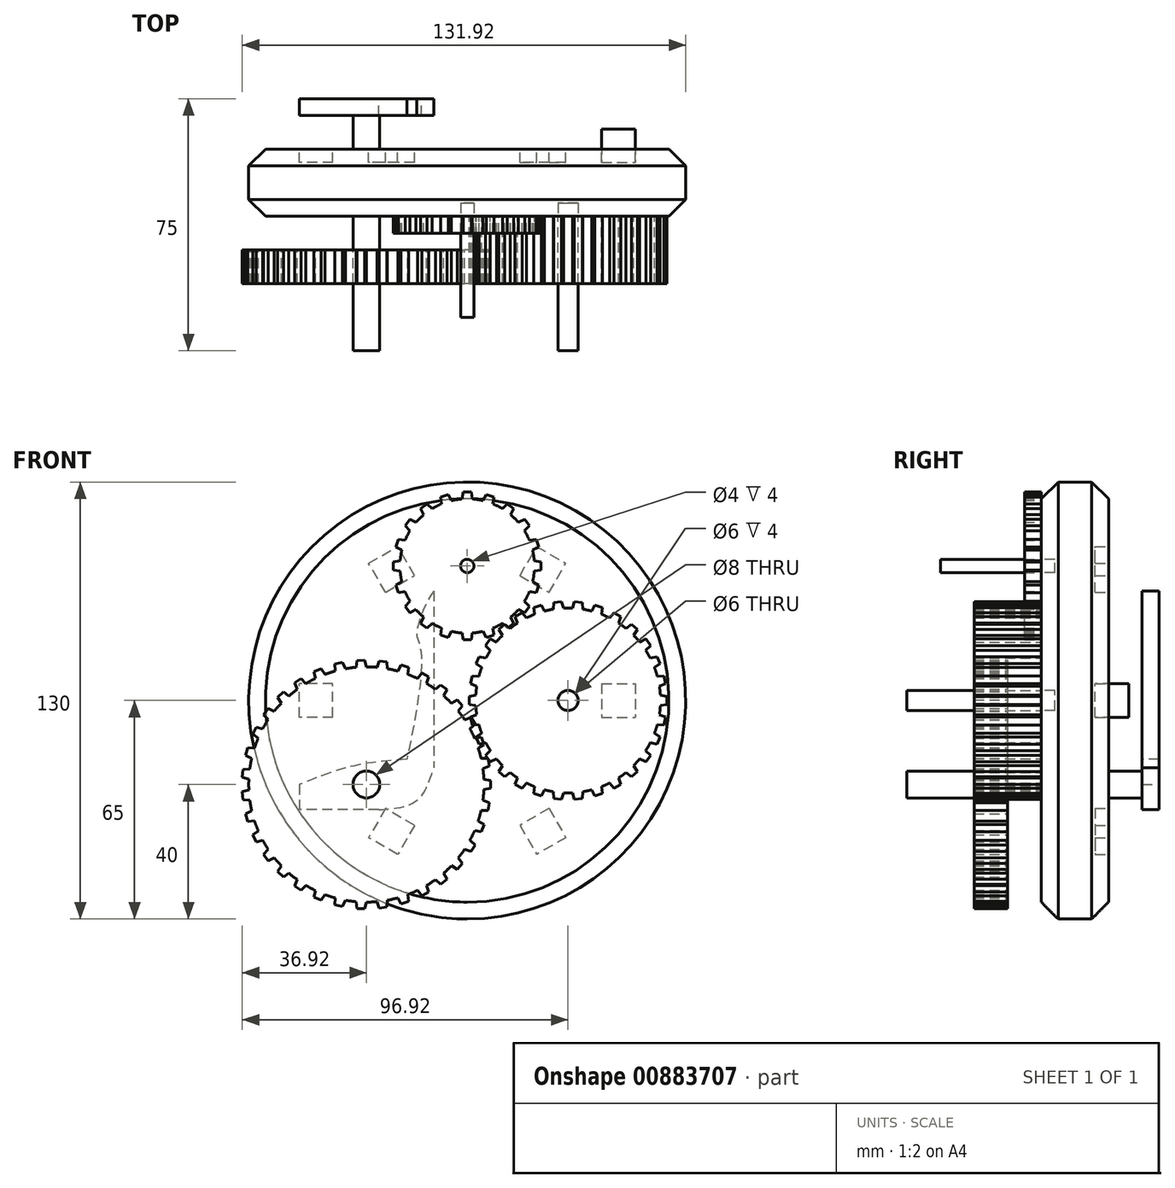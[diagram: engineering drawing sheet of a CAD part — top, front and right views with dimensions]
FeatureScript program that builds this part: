
annotation { "Feature Type Name" : "Feature", "Feature Type Description" : "" }
export const myFeature = defineFeature(function(context is Context, id is Id, definition is map)
    precondition{}
    {
        {
            var Q0;
            Q0=qCreatedBy(makeId("Front.planeOp"),FACE);
            var sketch = newSketch(context, id + "F0", { "sketchPlane" : qUnion([Q0])});
            skCircle(sketch, "E0", {"center": v(0, 0) * mm, "radius": 65 * mm});
            skSolve(sketch);
        }
        {
            var Q0;
            Q0 = qSketchRegion(id + "F0", true);
            extrude(context, id + "F1", {"entities" : qUnion([Q0]), "depth" : 20 * mm, "offsetDistance" : 25 * mm});
        }
        {
            var Q0;
            Q0=makeQuery(id+"F1.opExtrude","CAP_FACE",FACE,{"disambiguationData":[OSD([sQuery(id+"F0.wireOp",EDGE,"E0")])],"isStart":false});
            var sketch = newSketch(context, id + "F2", { "sketchPlane" : qUnion([Q0])});
            skCircle(sketch, "E1", {"center": v(0, 40) * mm, "radius": 20 * mm});
            skCircle(sketch, "E2.0", {"center": v(0, 40) * mm, "radius": 2 * mm});
            skLineSegment(sketch, "E3", {"start": v(0, 61.97) * mm, "end": v(1.18, 61.97) * mm});
            skLineSegment(sketch, "E4", {"start": v(1.18, 61.97) * mm, "end": v(1.54, 59.94) * mm});
            skLineSegment(sketch, "E5.MirrorCS", {"start": v(0, 61.97) * mm, "end": v(-1.18, 61.97) * mm});
            skLineSegment(sketch, "E6.MirrorCS", {"start": v(-1.18, 61.97) * mm, "end": v(-1.54, 59.94) * mm});
            skLineSegment(sketch, "E7.1.0", {"start": v(-7.9, 60.53) * mm, "end": v(-7.62, 58.5) * mm});
            skLineSegment(sketch, "E7.1.1", {"start": v(-6.79, 60.9) * mm, "end": v(-7.9, 60.53) * mm});
            skLineSegment(sketch, "E7.1.2", {"start": v(-6.79, 60.9) * mm, "end": v(-5.67, 61.26) * mm});
            skLineSegment(sketch, "E7.1.3", {"start": v(-5.67, 61.26) * mm, "end": v(-4.7, 59.44) * mm});
            skLineSegment(sketch, "E7.2.0", {"start": v(-13.87, 57.08) * mm, "end": v(-12.96, 55.23) * mm});
            skLineSegment(sketch, "E7.2.1", {"start": v(-12.91, 57.77) * mm, "end": v(-13.87, 57.08) * mm});
            skLineSegment(sketch, "E7.2.2", {"start": v(-12.91, 57.77) * mm, "end": v(-11.96, 58.47) * mm});
            skLineSegment(sketch, "E7.2.3", {"start": v(-11.96, 58.47) * mm, "end": v(-10.48, 57.04) * mm});
            skLineSegment(sketch, "E8.2.3.0", {"start": v(-18.47, 51.96) * mm, "end": v(-17.04, 50.48) * mm});
            skLineSegment(sketch, "E8.3.3.0", {"start": v(-17.77, 52.91) * mm, "end": v(-18.47, 51.96) * mm});
            skLineSegment(sketch, "E8.6.3.0", {"start": v(-17.77, 52.91) * mm, "end": v(-17.08, 53.87) * mm});
            skLineSegment(sketch, "E8.9.3.0", {"start": v(-17.08, 53.87) * mm, "end": v(-15.23, 52.96) * mm});
            skLineSegment(sketch, "E8.2.4.0", {"start": v(-21.26, 45.67) * mm, "end": v(-19.44, 44.7) * mm});
            skLineSegment(sketch, "E8.3.4.0", {"start": v(-20.9, 46.79) * mm, "end": v(-21.26, 45.67) * mm});
            skLineSegment(sketch, "E8.6.4.0", {"start": v(-20.9, 46.79) * mm, "end": v(-20.53, 47.9) * mm});
            skLineSegment(sketch, "E8.9.4.0", {"start": v(-20.53, 47.9) * mm, "end": v(-18.5, 47.62) * mm});
            skLineSegment(sketch, "E8.2.5.0", {"start": v(-21.97, 38.82) * mm, "end": v(-19.94, 38.46) * mm});
            skLineSegment(sketch, "E8.3.5.0", {"start": v(-21.97, 40) * mm, "end": v(-21.97, 38.82) * mm});
            skLineSegment(sketch, "E8.6.5.0", {"start": v(-21.97, 40) * mm, "end": v(-21.97, 41.18) * mm});
            skLineSegment(sketch, "E8.9.5.0", {"start": v(-21.97, 41.18) * mm, "end": v(-19.94, 41.54) * mm});
            skLineSegment(sketch, "E8.2.6.0", {"start": v(-20.53, 32.1) * mm, "end": v(-18.5, 32.38) * mm});
            skLineSegment(sketch, "E8.3.6.0", {"start": v(-20.9, 33.21) * mm, "end": v(-20.53, 32.1) * mm});
            skLineSegment(sketch, "E8.6.6.0", {"start": v(-20.9, 33.21) * mm, "end": v(-21.26, 34.33) * mm});
            skLineSegment(sketch, "E8.9.6.0", {"start": v(-21.26, 34.33) * mm, "end": v(-19.44, 35.3) * mm});
            skLineSegment(sketch, "E8.2.7.0", {"start": v(-17.08, 26.13) * mm, "end": v(-15.23, 27.04) * mm});
            skLineSegment(sketch, "E8.3.7.0", {"start": v(-17.77, 27.09) * mm, "end": v(-17.08, 26.13) * mm});
            skLineSegment(sketch, "E8.6.7.0", {"start": v(-17.77, 27.09) * mm, "end": v(-18.47, 28.04) * mm});
            skLineSegment(sketch, "E8.9.7.0", {"start": v(-18.47, 28.04) * mm, "end": v(-17.04, 29.52) * mm});
            skLineSegment(sketch, "E8.2.8.0", {"start": v(-11.96, 21.53) * mm, "end": v(-10.48, 22.96) * mm});
            skLineSegment(sketch, "E8.3.8.0", {"start": v(-12.91, 22.23) * mm, "end": v(-11.96, 21.53) * mm});
            skLineSegment(sketch, "E8.6.8.0", {"start": v(-12.91, 22.23) * mm, "end": v(-13.87, 22.92) * mm});
            skLineSegment(sketch, "E8.9.8.0", {"start": v(-13.87, 22.92) * mm, "end": v(-12.96, 24.77) * mm});
            skLineSegment(sketch, "E8.2.9.0", {"start": v(-5.67, 18.74) * mm, "end": v(-4.7, 20.56) * mm});
            skLineSegment(sketch, "E8.3.9.0", {"start": v(-6.79, 19.1) * mm, "end": v(-5.67, 18.74) * mm});
            skLineSegment(sketch, "E8.6.9.0", {"start": v(-6.79, 19.1) * mm, "end": v(-7.9, 19.47) * mm});
            skLineSegment(sketch, "E8.9.9.0", {"start": v(-7.9, 19.47) * mm, "end": v(-7.62, 21.5) * mm});
            skLineSegment(sketch, "E9.2.10.0", {"start": v(1.18, 18.03) * mm, "end": v(1.54, 20.06) * mm});
            skLineSegment(sketch, "E9.3.10.0", {"start": v(0, 18.03) * mm, "end": v(1.18, 18.03) * mm});
            skLineSegment(sketch, "E9.6.10.0", {"start": v(0, 18.03) * mm, "end": v(-1.18, 18.03) * mm});
            skLineSegment(sketch, "E9.9.10.0", {"start": v(-1.18, 18.03) * mm, "end": v(-1.54, 20.06) * mm});
            skLineSegment(sketch, "E9.2.11.0", {"start": v(7.9, 19.47) * mm, "end": v(7.62, 21.5) * mm});
            skLineSegment(sketch, "E9.3.11.0", {"start": v(6.79, 19.1) * mm, "end": v(7.9, 19.47) * mm});
            skLineSegment(sketch, "E9.6.11.0", {"start": v(6.79, 19.1) * mm, "end": v(5.67, 18.74) * mm});
            skLineSegment(sketch, "E9.9.11.0", {"start": v(5.67, 18.74) * mm, "end": v(4.7, 20.56) * mm});
            skLineSegment(sketch, "E9.2.12.0", {"start": v(13.87, 22.92) * mm, "end": v(12.96, 24.77) * mm});
            skLineSegment(sketch, "E9.3.12.0", {"start": v(12.91, 22.23) * mm, "end": v(13.87, 22.92) * mm});
            skLineSegment(sketch, "E9.6.12.0", {"start": v(12.91, 22.23) * mm, "end": v(11.96, 21.53) * mm});
            skLineSegment(sketch, "E9.9.12.0", {"start": v(11.96, 21.53) * mm, "end": v(10.48, 22.96) * mm});
            skLineSegment(sketch, "E9.2.13.0", {"start": v(18.47, 28.04) * mm, "end": v(17.04, 29.52) * mm});
            skLineSegment(sketch, "E9.3.13.0", {"start": v(17.77, 27.09) * mm, "end": v(18.47, 28.04) * mm});
            skLineSegment(sketch, "E9.6.13.0", {"start": v(17.77, 27.09) * mm, "end": v(17.08, 26.13) * mm});
            skLineSegment(sketch, "E9.9.13.0", {"start": v(17.08, 26.13) * mm, "end": v(15.23, 27.04) * mm});
            skLineSegment(sketch, "E9.2.14.0", {"start": v(21.26, 34.33) * mm, "end": v(19.44, 35.3) * mm});
            skLineSegment(sketch, "E9.3.14.0", {"start": v(20.9, 33.21) * mm, "end": v(21.26, 34.33) * mm});
            skLineSegment(sketch, "E9.6.14.0", {"start": v(20.9, 33.21) * mm, "end": v(20.53, 32.1) * mm});
            skLineSegment(sketch, "E9.9.14.0", {"start": v(20.53, 32.1) * mm, "end": v(18.5, 32.38) * mm});
            skLineSegment(sketch, "E9.2.15.0", {"start": v(21.97, 41.18) * mm, "end": v(19.94, 41.54) * mm});
            skLineSegment(sketch, "E9.3.15.0", {"start": v(21.97, 40) * mm, "end": v(21.97, 41.18) * mm});
            skLineSegment(sketch, "E9.6.15.0", {"start": v(21.97, 40) * mm, "end": v(21.97, 38.82) * mm});
            skLineSegment(sketch, "E9.9.15.0", {"start": v(21.97, 38.82) * mm, "end": v(19.94, 38.46) * mm});
            skLineSegment(sketch, "E9.2.16.0", {"start": v(20.53, 47.9) * mm, "end": v(18.5, 47.62) * mm});
            skLineSegment(sketch, "E9.3.16.0", {"start": v(20.9, 46.79) * mm, "end": v(20.53, 47.9) * mm});
            skLineSegment(sketch, "E9.6.16.0", {"start": v(20.9, 46.79) * mm, "end": v(21.26, 45.67) * mm});
            skLineSegment(sketch, "E9.9.16.0", {"start": v(21.26, 45.67) * mm, "end": v(19.44, 44.7) * mm});
            skLineSegment(sketch, "E9.2.17.0", {"start": v(17.08, 53.87) * mm, "end": v(15.23, 52.96) * mm});
            skLineSegment(sketch, "E9.3.17.0", {"start": v(17.77, 52.91) * mm, "end": v(17.08, 53.87) * mm});
            skLineSegment(sketch, "E9.6.17.0", {"start": v(17.77, 52.91) * mm, "end": v(18.47, 51.96) * mm});
            skLineSegment(sketch, "E9.9.17.0", {"start": v(18.47, 51.96) * mm, "end": v(17.04, 50.48) * mm});
            skLineSegment(sketch, "E9.2.18.0", {"start": v(11.96, 58.47) * mm, "end": v(10.48, 57.04) * mm});
            skLineSegment(sketch, "E9.3.18.0", {"start": v(12.91, 57.77) * mm, "end": v(11.96, 58.47) * mm});
            skLineSegment(sketch, "E9.6.18.0", {"start": v(12.91, 57.77) * mm, "end": v(13.87, 57.08) * mm});
            skLineSegment(sketch, "E9.9.18.0", {"start": v(13.87, 57.08) * mm, "end": v(12.96, 55.23) * mm});
            skLineSegment(sketch, "E9.2.19.0", {"start": v(5.67, 61.26) * mm, "end": v(4.7, 59.44) * mm});
            skLineSegment(sketch, "E9.3.19.0", {"start": v(6.79, 60.9) * mm, "end": v(5.67, 61.26) * mm});
            skLineSegment(sketch, "E9.6.19.0", {"start": v(6.79, 60.9) * mm, "end": v(7.9, 60.53) * mm});
            skLineSegment(sketch, "E9.9.19.0", {"start": v(7.9, 60.53) * mm, "end": v(7.62, 58.5) * mm});
            skSolve(sketch);
        }
        {
            var Q0;
            Q0 = qSketchRegion(id + "F2", true);
            extrude(context, id + "F3", {"entities" : qUnion([Q0]), "depth" : 5 * mm, "offsetDistance" : 25 * mm});
        }
        {
            var Q0;
            Q0=makeQuery(id+"F1.opExtrude","CAP_FACE",FACE,{"disambiguationData":[OSD([sQuery(id+"F0.wireOp",EDGE,"E0")])],"isStart":false});
            var sketch = newSketch(context, id + "F4", { "sketchPlane" : qUnion([Q0])});
            skCircle(sketch, "E10.0", {"center": v(0, 40) * mm, "radius": 2 * mm});
            skSolve(sketch);
        }
        {
            var Q0;
            Q0 = qSketchRegion(id + "F4", true);
            extrude(context, id + "F5", {"entities" : qUnion([Q0]), "depth" : 30 * mm, "offsetDistance" : 25 * mm});
        }
        {
            var Q0;
            Q0=makeQuery(id+"F1.opExtrude","CAP_FACE",FACE,{"disambiguationData":[OSD([sQuery(id+"F0.wireOp",EDGE,"E0")])],"isStart":false});
            var sketch = newSketch(context, id + "F6", { "sketchPlane" : qUnion([Q0])});
            skCircle(sketch, "E11", {"center": v(30, 0) * mm, "radius": 27.5 * mm});
            skLineSegment(sketch, "E12", {"start": v(59.46, 0) * mm, "end": v(59.46, -1.18) * mm});
            skLineSegment(sketch, "E13", {"start": v(59.46, -1.18) * mm, "end": v(57.46, -1.53) * mm});
            skLineSegment(sketch, "E14.MirrorCS", {"start": v(59.46, 0) * mm, "end": v(59.46, 1.18) * mm});
            skLineSegment(sketch, "E15.MirrorCS", {"start": v(59.46, 1.18) * mm, "end": v(57.46, 1.53) * mm});
            skLineSegment(sketch, "E16.1.0", {"start": v(58.57, 7.28) * mm, "end": v(56.54, 7.2) * mm});
            skLineSegment(sketch, "E16.1.1", {"start": v(58.81, 6.12) * mm, "end": v(58.57, 7.28) * mm});
            skLineSegment(sketch, "E16.1.2", {"start": v(58.81, 6.12) * mm, "end": v(59.06, 4.97) * mm});
            skLineSegment(sketch, "E16.1.3", {"start": v(59.06, 4.97) * mm, "end": v(57.18, 4.21) * mm});
            skLineSegment(sketch, "E16.2.0", {"start": v(56.43, 13.06) * mm, "end": v(54.46, 12.57) * mm});
            skLineSegment(sketch, "E16.2.1", {"start": v(56.91, 11.98) * mm, "end": v(56.43, 13.06) * mm});
            skLineSegment(sketch, "E16.2.2", {"start": v(56.91, 11.98) * mm, "end": v(57.39, 10.9) * mm});
            skLineSegment(sketch, "E16.2.3", {"start": v(57.39, 10.9) * mm, "end": v(55.7, 9.77) * mm});
            skLineSegment(sketch, "E17.2.3.0", {"start": v(53.14, 18.27) * mm, "end": v(51.31, 17.38) * mm});
            skLineSegment(sketch, "E17.3.3.0", {"start": v(53.83, 17.31) * mm, "end": v(53.14, 18.27) * mm});
            skLineSegment(sketch, "E17.6.3.0", {"start": v(53.83, 17.31) * mm, "end": v(54.52, 16.36) * mm});
            skLineSegment(sketch, "E17.9.3.0", {"start": v(54.52, 16.36) * mm, "end": v(53.11, 14.9) * mm});
            skLineSegment(sketch, "E17.2.4.0", {"start": v(48.84, 22.68) * mm, "end": v(47.24, 21.43) * mm});
            skLineSegment(sketch, "E17.3.4.0", {"start": v(49.71, 21.9) * mm, "end": v(48.84, 22.68) * mm});
            skLineSegment(sketch, "E17.6.4.0", {"start": v(49.71, 21.9) * mm, "end": v(50.59, 21.1) * mm});
            skLineSegment(sketch, "E17.9.4.0", {"start": v(50.59, 21.1) * mm, "end": v(49.51, 19.38) * mm});
            skLineSegment(sketch, "E17.2.5.0", {"start": v(43.7, 26.1) * mm, "end": v(42.4, 24.54) * mm});
            skLineSegment(sketch, "E17.3.5.0", {"start": v(44.73, 25.51) * mm, "end": v(43.7, 26.1) * mm});
            skLineSegment(sketch, "E17.6.5.0", {"start": v(44.73, 25.51) * mm, "end": v(45.75, 24.92) * mm});
            skLineSegment(sketch, "E17.9.5.0", {"start": v(45.75, 24.92) * mm, "end": v(45.05, 23.01) * mm});
            skLineSegment(sketch, "E17.2.6.0", {"start": v(37.98, 28.38) * mm, "end": v(37.03, 26.59) * mm});
            skLineSegment(sketch, "E17.3.6.0", {"start": v(39.1, 28.02) * mm, "end": v(37.98, 28.38) * mm});
            skLineSegment(sketch, "E17.6.6.0", {"start": v(39.1, 28.02) * mm, "end": v(40.22, 27.65) * mm});
            skLineSegment(sketch, "E17.9.6.0", {"start": v(40.22, 27.65) * mm, "end": v(39.94, 25.64) * mm});
            skLineSegment(sketch, "E17.2.7.0", {"start": v(31.9, 29.42) * mm, "end": v(31.35, 27.47) * mm});
            skLineSegment(sketch, "E17.3.7.0", {"start": v(33.08, 29.3) * mm, "end": v(31.9, 29.42) * mm});
            skLineSegment(sketch, "E17.6.7.0", {"start": v(33.08, 29.3) * mm, "end": v(34.25, 29.17) * mm});
            skLineSegment(sketch, "E17.9.7.0", {"start": v(34.25, 29.17) * mm, "end": v(34.4, 27.15) * mm});
            skLineSegment(sketch, "E17.2.8.0", {"start": v(25.75, 29.17) * mm, "end": v(25.6, 27.15) * mm});
            skLineSegment(sketch, "E17.3.8.0", {"start": v(26.92, 29.3) * mm, "end": v(25.75, 29.17) * mm});
            skLineSegment(sketch, "E17.6.8.0", {"start": v(26.92, 29.3) * mm, "end": v(28.1, 29.42) * mm});
            skLineSegment(sketch, "E17.9.8.0", {"start": v(28.1, 29.42) * mm, "end": v(28.65, 27.47) * mm});
            skLineSegment(sketch, "E17.2.9.0", {"start": v(19.78, 27.65) * mm, "end": v(20.06, 25.64) * mm});
            skLineSegment(sketch, "E17.3.9.0", {"start": v(20.9, 28.02) * mm, "end": v(19.78, 27.65) * mm});
            skLineSegment(sketch, "E17.6.9.0", {"start": v(20.9, 28.02) * mm, "end": v(22.02, 28.38) * mm});
            skLineSegment(sketch, "E17.9.9.0", {"start": v(22.02, 28.38) * mm, "end": v(22.97, 26.59) * mm});
            skLineSegment(sketch, "E17.2.10.0", {"start": v(14.25, 24.92) * mm, "end": v(14.95, 23.01) * mm});
            skLineSegment(sketch, "E17.3.10.0", {"start": v(15.27, 25.51) * mm, "end": v(14.25, 24.92) * mm});
            skLineSegment(sketch, "E17.6.10.0", {"start": v(15.27, 25.51) * mm, "end": v(16.3, 26.1) * mm});
            skLineSegment(sketch, "E17.9.10.0", {"start": v(16.3, 26.1) * mm, "end": v(17.6, 24.54) * mm});
            skLineSegment(sketch, "E17.2.11.0", {"start": v(9.41, 21.1) * mm, "end": v(10.49, 19.38) * mm});
            skLineSegment(sketch, "E17.3.11.0", {"start": v(10.29, 21.9) * mm, "end": v(9.41, 21.1) * mm});
            skLineSegment(sketch, "E17.6.11.0", {"start": v(10.29, 21.9) * mm, "end": v(11.16, 22.68) * mm});
            skLineSegment(sketch, "E17.9.11.0", {"start": v(11.16, 22.68) * mm, "end": v(12.76, 21.43) * mm});
            skLineSegment(sketch, "E17.2.12.0", {"start": v(5.48, 16.36) * mm, "end": v(6.89, 14.9) * mm});
            skLineSegment(sketch, "E17.3.12.0", {"start": v(6.17, 17.31) * mm, "end": v(5.48, 16.36) * mm});
            skLineSegment(sketch, "E17.6.12.0", {"start": v(6.17, 17.31) * mm, "end": v(6.86, 18.27) * mm});
            skLineSegment(sketch, "E17.9.12.0", {"start": v(6.86, 18.27) * mm, "end": v(8.69, 17.38) * mm});
            skLineSegment(sketch, "E17.2.13.0", {"start": v(2.61, 10.9) * mm, "end": v(4.3, 9.77) * mm});
            skLineSegment(sketch, "E17.3.13.0", {"start": v(3.09, 11.98) * mm, "end": v(2.61, 10.9) * mm});
            skLineSegment(sketch, "E17.6.13.0", {"start": v(3.09, 11.98) * mm, "end": v(3.57, 13.06) * mm});
            skLineSegment(sketch, "E17.9.13.0", {"start": v(3.57, 13.06) * mm, "end": v(5.54, 12.57) * mm});
            skLineSegment(sketch, "E17.2.14.0", {"start": v(0.94, 4.97) * mm, "end": v(2.82, 4.21) * mm});
            skLineSegment(sketch, "E17.3.14.0", {"start": v(1.19, 6.12) * mm, "end": v(0.94, 4.97) * mm});
            skLineSegment(sketch, "E17.6.14.0", {"start": v(1.19, 6.12) * mm, "end": v(1.43, 7.28) * mm});
            skLineSegment(sketch, "E17.9.14.0", {"start": v(1.43, 7.28) * mm, "end": v(3.46, 7.2) * mm});
            skLineSegment(sketch, "E17.2.15.0", {"start": v(0.54, -1.18) * mm, "end": v(2.54, -1.53) * mm});
            skLineSegment(sketch, "E17.3.15.0", {"start": v(0.54, 0) * mm, "end": v(0.54, -1.18) * mm});
            skLineSegment(sketch, "E17.6.15.0", {"start": v(0.54, 0) * mm, "end": v(0.54, 1.18) * mm});
            skLineSegment(sketch, "E17.9.15.0", {"start": v(0.54, 1.18) * mm, "end": v(2.54, 1.53) * mm});
            skLineSegment(sketch, "E17.2.16.0", {"start": v(1.43, -7.28) * mm, "end": v(3.46, -7.2) * mm});
            skLineSegment(sketch, "E17.3.16.0", {"start": v(1.19, -6.12) * mm, "end": v(1.43, -7.28) * mm});
            skLineSegment(sketch, "E17.6.16.0", {"start": v(1.19, -6.12) * mm, "end": v(0.94, -4.97) * mm});
            skLineSegment(sketch, "E17.9.16.0", {"start": v(0.94, -4.97) * mm, "end": v(2.82, -4.21) * mm});
            skLineSegment(sketch, "E17.2.17.0", {"start": v(3.57, -13.06) * mm, "end": v(5.54, -12.57) * mm});
            skLineSegment(sketch, "E17.3.17.0", {"start": v(3.09, -11.98) * mm, "end": v(3.57, -13.06) * mm});
            skLineSegment(sketch, "E17.6.17.0", {"start": v(3.09, -11.98) * mm, "end": v(2.61, -10.9) * mm});
            skLineSegment(sketch, "E17.9.17.0", {"start": v(2.61, -10.9) * mm, "end": v(4.3, -9.77) * mm});
            skLineSegment(sketch, "E17.2.18.0", {"start": v(6.86, -18.27) * mm, "end": v(8.69, -17.38) * mm});
            skLineSegment(sketch, "E17.3.18.0", {"start": v(6.17, -17.31) * mm, "end": v(6.86, -18.27) * mm});
            skLineSegment(sketch, "E17.6.18.0", {"start": v(6.17, -17.31) * mm, "end": v(5.48, -16.36) * mm});
            skLineSegment(sketch, "E17.9.18.0", {"start": v(5.48, -16.36) * mm, "end": v(6.89, -14.9) * mm});
            skLineSegment(sketch, "E17.2.19.0", {"start": v(11.16, -22.68) * mm, "end": v(12.76, -21.43) * mm});
            skLineSegment(sketch, "E17.3.19.0", {"start": v(10.29, -21.9) * mm, "end": v(11.16, -22.68) * mm});
            skLineSegment(sketch, "E17.6.19.0", {"start": v(10.29, -21.9) * mm, "end": v(9.41, -21.1) * mm});
            skLineSegment(sketch, "E17.9.19.0", {"start": v(9.41, -21.1) * mm, "end": v(10.49, -19.38) * mm});
            skLineSegment(sketch, "E18.2.20.0", {"start": v(16.3, -26.1) * mm, "end": v(17.6, -24.54) * mm});
            skLineSegment(sketch, "E18.3.20.0", {"start": v(15.27, -25.51) * mm, "end": v(16.3, -26.1) * mm});
            skLineSegment(sketch, "E18.6.20.0", {"start": v(15.27, -25.51) * mm, "end": v(14.25, -24.92) * mm});
            skLineSegment(sketch, "E18.9.20.0", {"start": v(14.25, -24.92) * mm, "end": v(14.95, -23.01) * mm});
            skLineSegment(sketch, "E18.2.21.0", {"start": v(22.02, -28.38) * mm, "end": v(22.97, -26.59) * mm});
            skLineSegment(sketch, "E18.3.21.0", {"start": v(20.9, -28.02) * mm, "end": v(22.02, -28.38) * mm});
            skLineSegment(sketch, "E18.6.21.0", {"start": v(20.9, -28.02) * mm, "end": v(19.78, -27.65) * mm});
            skLineSegment(sketch, "E18.9.21.0", {"start": v(19.78, -27.65) * mm, "end": v(20.06, -25.64) * mm});
            skLineSegment(sketch, "E18.2.22.0", {"start": v(28.1, -29.42) * mm, "end": v(28.65, -27.47) * mm});
            skLineSegment(sketch, "E18.3.22.0", {"start": v(26.92, -29.3) * mm, "end": v(28.1, -29.42) * mm});
            skLineSegment(sketch, "E18.6.22.0", {"start": v(26.92, -29.3) * mm, "end": v(25.75, -29.17) * mm});
            skLineSegment(sketch, "E18.9.22.0", {"start": v(25.75, -29.17) * mm, "end": v(25.6, -27.15) * mm});
            skLineSegment(sketch, "E18.2.23.0", {"start": v(34.25, -29.17) * mm, "end": v(34.4, -27.15) * mm});
            skLineSegment(sketch, "E18.3.23.0", {"start": v(33.08, -29.3) * mm, "end": v(34.25, -29.17) * mm});
            skLineSegment(sketch, "E18.6.23.0", {"start": v(33.08, -29.3) * mm, "end": v(31.9, -29.42) * mm});
            skLineSegment(sketch, "E18.9.23.0", {"start": v(31.9, -29.42) * mm, "end": v(31.35, -27.47) * mm});
            skLineSegment(sketch, "E18.2.24.0", {"start": v(40.22, -27.65) * mm, "end": v(39.94, -25.64) * mm});
            skLineSegment(sketch, "E18.3.24.0", {"start": v(39.1, -28.02) * mm, "end": v(40.22, -27.65) * mm});
            skLineSegment(sketch, "E18.6.24.0", {"start": v(39.1, -28.02) * mm, "end": v(37.98, -28.38) * mm});
            skLineSegment(sketch, "E18.9.24.0", {"start": v(37.98, -28.38) * mm, "end": v(37.03, -26.59) * mm});
            skLineSegment(sketch, "E19.2.25.0", {"start": v(45.75, -24.92) * mm, "end": v(45.05, -23.01) * mm});
            skLineSegment(sketch, "E19.3.25.0", {"start": v(44.73, -25.51) * mm, "end": v(45.75, -24.92) * mm});
            skLineSegment(sketch, "E19.6.25.0", {"start": v(44.73, -25.51) * mm, "end": v(43.7, -26.1) * mm});
            skLineSegment(sketch, "E19.9.25.0", {"start": v(43.7, -26.1) * mm, "end": v(42.4, -24.54) * mm});
            skLineSegment(sketch, "E19.2.26.0", {"start": v(50.59, -21.1) * mm, "end": v(49.51, -19.38) * mm});
            skLineSegment(sketch, "E19.3.26.0", {"start": v(49.71, -21.9) * mm, "end": v(50.59, -21.1) * mm});
            skLineSegment(sketch, "E19.6.26.0", {"start": v(49.71, -21.9) * mm, "end": v(48.84, -22.68) * mm});
            skLineSegment(sketch, "E19.9.26.0", {"start": v(48.84, -22.68) * mm, "end": v(47.24, -21.43) * mm});
            skLineSegment(sketch, "E19.2.27.0", {"start": v(54.52, -16.36) * mm, "end": v(53.11, -14.9) * mm});
            skLineSegment(sketch, "E19.3.27.0", {"start": v(53.83, -17.31) * mm, "end": v(54.52, -16.36) * mm});
            skLineSegment(sketch, "E19.6.27.0", {"start": v(53.83, -17.31) * mm, "end": v(53.14, -18.27) * mm});
            skLineSegment(sketch, "E19.9.27.0", {"start": v(53.14, -18.27) * mm, "end": v(51.31, -17.38) * mm});
            skLineSegment(sketch, "E20.2.28.0", {"start": v(57.39, -10.9) * mm, "end": v(55.7, -9.77) * mm});
            skLineSegment(sketch, "E20.3.28.0", {"start": v(56.91, -11.98) * mm, "end": v(57.39, -10.9) * mm});
            skLineSegment(sketch, "E20.6.28.0", {"start": v(56.91, -11.98) * mm, "end": v(56.43, -13.06) * mm});
            skLineSegment(sketch, "E20.9.28.0", {"start": v(56.43, -13.06) * mm, "end": v(54.46, -12.57) * mm});
            skLineSegment(sketch, "E20.2.29.0", {"start": v(59.06, -4.97) * mm, "end": v(57.18, -4.21) * mm});
            skLineSegment(sketch, "E20.3.29.0", {"start": v(58.81, -6.12) * mm, "end": v(59.06, -4.97) * mm});
            skLineSegment(sketch, "E20.6.29.0", {"start": v(58.81, -6.12) * mm, "end": v(58.57, -7.28) * mm});
            skLineSegment(sketch, "E20.9.29.0", {"start": v(58.57, -7.28) * mm, "end": v(56.54, -7.2) * mm});
            skCircle(sketch, "E21", {"center": v(30, 0) * mm, "radius": 3 * mm});
            skSolve(sketch);
        }
        {
            var Q0;
            Q0 = qSketchRegion(id + "F6", true);
            extrude(context, id + "F7", {"entities" : qUnion([Q0]), "depth" : 20 * mm, "offsetDistance" : 25 * mm});
        }
        {
            var Q0;
            Q0=makeQuery(id+"F1.opExtrude","CAP_FACE",FACE,{"disambiguationData":[OSD([sQuery(id+"F0.wireOp",EDGE,"E0")])],"isStart":false});
            var sketch = newSketch(context, id + "F8", { "sketchPlane" : qUnion([Q0])});
            skCircle(sketch, "E22.0", {"center": v(30, 0) * mm, "radius": 3 * mm});
            skSolve(sketch);
        }
        {
            var Q0;
            Q0 = qSketchRegion(id + "F8", true);
            extrude(context, id + "F9", {"entities" : qUnion([Q0]), "depth" : 40 * mm, "offsetDistance" : 25 * mm});
        }
        {
            var Q0;
            Q0=qCreatedBy(makeId("Front.planeOp"),FACE);
            cPlane(context, id + "F10", {"entities" : qUnion([Q0]), "cplaneType" : CPlaneType.OFFSET, "offset" : 30 * mm, "width" : 150 * mm, "height" : 150 * mm});
        }
        {
            var Q0;
            Q0=qCreatedBy(id+"F10.planeOp",FACE);
            var sketch = newSketch(context, id + "F11", { "sketchPlane" : qUnion([Q0])});
            skCircle(sketch, "E23", {"center": v(-30, -25) * mm, "radius": 35 * mm});
            skLineSegment(sketch, "E24", {"start": v(-30, -25) * mm, "end": v(5, -25) * mm, "construction": true});
            skLineSegment(sketch, "E25", {"start": v(5, -25) * mm, "end": v(6.97, -25) * mm});
            skLineSegment(sketch, "E26", {"start": v(6.97, -25) * mm, "end": v(6.97, -26.18) * mm});
            skLineSegment(sketch, "E27", {"start": v(6.97, -26.18) * mm, "end": v(4.97, -26.53) * mm});
            skLineSegment(sketch, "E28.MirrorCS", {"start": v(6.97, -25) * mm, "end": v(6.97, -23.82) * mm});
            skLineSegment(sketch, "E29.MirrorCS", {"start": v(6.97, -23.82) * mm, "end": v(4.97, -23.47) * mm});
            skLineSegment(sketch, "E30.1.0", {"start": v(6.16, -17.24) * mm, "end": v(4.13, -17.25) * mm});
            skLineSegment(sketch, "E30.1.1", {"start": v(6.37, -18.4) * mm, "end": v(6.16, -17.24) * mm});
            skLineSegment(sketch, "E30.1.2", {"start": v(6.37, -18.4) * mm, "end": v(6.58, -19.56) * mm});
            skLineSegment(sketch, "E30.1.3", {"start": v(6.58, -19.56) * mm, "end": v(4.68, -20.26) * mm});
            skLineSegment(sketch, "E30.2.0", {"start": v(4.2, -10.9) * mm, "end": v(2.2, -11.28) * mm});
            skLineSegment(sketch, "E30.2.1", {"start": v(4.6, -12.01) * mm, "end": v(4.2, -10.9) * mm});
            skLineSegment(sketch, "E30.2.2", {"start": v(4.6, -12.01) * mm, "end": v(5.02, -13.11) * mm});
            skLineSegment(sketch, "E30.2.3", {"start": v(5.02, -13.11) * mm, "end": v(3.27, -14.15) * mm});
            skLineSegment(sketch, "E31.2.3.0", {"start": v(1.13, -5.03) * mm, "end": v(-0.77, -5.75) * mm});
            skLineSegment(sketch, "E31.3.3.0", {"start": v(1.73, -6.04) * mm, "end": v(1.13, -5.03) * mm});
            skLineSegment(sketch, "E31.6.3.0", {"start": v(1.73, -6.04) * mm, "end": v(2.34, -7.05) * mm});
            skLineSegment(sketch, "E31.9.3.0", {"start": v(2.34, -7.05) * mm, "end": v(0.8, -8.38) * mm});
            skLineSegment(sketch, "E31.2.4.0", {"start": v(-2.94, 0.2) * mm, "end": v(-4.67, -0.84) * mm});
            skLineSegment(sketch, "E31.3.4.0", {"start": v(-2.16, -0.68) * mm, "end": v(-2.94, 0.2) * mm});
            skLineSegment(sketch, "E31.6.4.0", {"start": v(-2.16, -0.68) * mm, "end": v(-1.39, -1.57) * mm});
            skLineSegment(sketch, "E31.9.4.0", {"start": v(-1.39, -1.57) * mm, "end": v(-2.66, -3.15) * mm});
            skLineSegment(sketch, "E31.2.5.0", {"start": v(-7.87, 4.64) * mm, "end": v(-9.4, 3.3) * mm});
            skLineSegment(sketch, "E31.3.5.0", {"start": v(-6.95, 3.9) * mm, "end": v(-7.87, 4.64) * mm});
            skLineSegment(sketch, "E31.6.5.0", {"start": v(-6.95, 3.9) * mm, "end": v(-6.03, 3.17) * mm});
            skLineSegment(sketch, "E31.9.5.0", {"start": v(-6.03, 3.17) * mm, "end": v(-7, 1.38) * mm});
            skLineSegment(sketch, "E31.2.6.0", {"start": v(-13.52, 8.11) * mm, "end": v(-14.78, 6.52) * mm});
            skLineSegment(sketch, "E31.3.6.0", {"start": v(-12.48, 7.55) * mm, "end": v(-13.52, 8.11) * mm});
            skLineSegment(sketch, "E31.6.6.0", {"start": v(-12.48, 7.55) * mm, "end": v(-11.45, 7) * mm});
            skLineSegment(sketch, "E31.9.6.0", {"start": v(-11.45, 7) * mm, "end": v(-12.08, 5.07) * mm});
            skLineSegment(sketch, "E31.2.7.0", {"start": v(-19.7, 10.52) * mm, "end": v(-20.65, 8.73) * mm});
            skLineSegment(sketch, "E31.3.7.0", {"start": v(-18.58, 10.16) * mm, "end": v(-19.7, 10.52) * mm});
            skLineSegment(sketch, "E31.6.7.0", {"start": v(-18.58, 10.16) * mm, "end": v(-17.46, 9.8) * mm});
            skLineSegment(sketch, "E31.9.7.0", {"start": v(-17.46, 9.8) * mm, "end": v(-17.74, 7.78) * mm});
            skLineSegment(sketch, "E31.2.8.0", {"start": v(-26.2, 11.8) * mm, "end": v(-26.82, 9.86) * mm});
            skLineSegment(sketch, "E31.3.8.0", {"start": v(-25.04, 11.63) * mm, "end": v(-26.2, 11.8) * mm});
            skLineSegment(sketch, "E31.6.8.0", {"start": v(-25.04, 11.63) * mm, "end": v(-23.87, 11.47) * mm});
            skLineSegment(sketch, "E31.9.8.0", {"start": v(-23.87, 11.47) * mm, "end": v(-23.79, 9.44) * mm});
            skLineSegment(sketch, "E31.2.9.0", {"start": v(-32.84, 11.88) * mm, "end": v(-33.1, 9.86) * mm});
            skLineSegment(sketch, "E31.3.9.0", {"start": v(-31.66, 11.93) * mm, "end": v(-32.84, 11.88) * mm});
            skLineSegment(sketch, "E31.6.9.0", {"start": v(-31.66, 11.93) * mm, "end": v(-30.48, 11.98) * mm});
            skLineSegment(sketch, "E31.9.9.0", {"start": v(-30.48, 11.98) * mm, "end": v(-30.04, 10) * mm});
            skLineSegment(sketch, "E31.2.10.0", {"start": v(-39.37, 10.78) * mm, "end": v(-39.27, 8.75) * mm});
            skLineSegment(sketch, "E31.3.10.0", {"start": v(-38.23, 11.04) * mm, "end": v(-39.37, 10.78) * mm});
            skLineSegment(sketch, "E31.6.10.0", {"start": v(-38.23, 11.04) * mm, "end": v(-37.08, 11.3) * mm});
            skLineSegment(sketch, "E31.9.10.0", {"start": v(-37.08, 11.3) * mm, "end": v(-36.29, 9.43) * mm});
            skLineSegment(sketch, "E31.2.11.0", {"start": v(-45.61, 8.53) * mm, "end": v(-45.15, 6.55) * mm});
            skLineSegment(sketch, "E31.3.11.0", {"start": v(-44.53, 9) * mm, "end": v(-45.61, 8.53) * mm});
            skLineSegment(sketch, "E31.6.11.0", {"start": v(-44.53, 9) * mm, "end": v(-43.45, 9.45) * mm});
            skLineSegment(sketch, "E31.9.11.0", {"start": v(-43.45, 9.45) * mm, "end": v(-42.34, 7.75) * mm});
            skLineSegment(sketch, "E31.2.12.0", {"start": v(-51.35, 5.2) * mm, "end": v(-50.54, 3.34) * mm});
            skLineSegment(sketch, "E31.3.12.0", {"start": v(-50.36, 5.85) * mm, "end": v(-51.35, 5.2) * mm});
            skLineSegment(sketch, "E31.6.12.0", {"start": v(-50.36, 5.85) * mm, "end": v(-49.38, 6.5) * mm});
            skLineSegment(sketch, "E31.9.12.0", {"start": v(-49.38, 6.5) * mm, "end": v(-47.99, 5.03) * mm});
            skLineSegment(sketch, "E31.2.13.0", {"start": v(-56.4, 0.9) * mm, "end": v(-55.27, -0.78) * mm});
            skLineSegment(sketch, "E31.3.13.0", {"start": v(-55.55, 1.72) * mm, "end": v(-56.4, 0.9) * mm});
            skLineSegment(sketch, "E31.6.13.0", {"start": v(-55.55, 1.72) * mm, "end": v(-54.7, 2.53) * mm});
            skLineSegment(sketch, "E31.9.13.0", {"start": v(-54.7, 2.53) * mm, "end": v(-53.06, 1.33) * mm});
            skLineSegment(sketch, "E31.2.14.0", {"start": v(-60.6, -4.22) * mm, "end": v(-59.19, -5.69) * mm});
            skLineSegment(sketch, "E31.3.14.0", {"start": v(-59.9, -3.27) * mm, "end": v(-60.6, -4.22) * mm});
            skLineSegment(sketch, "E31.6.14.0", {"start": v(-59.9, -3.27) * mm, "end": v(-59.21, -2.32) * mm});
            skLineSegment(sketch, "E31.9.14.0", {"start": v(-59.21, -2.32) * mm, "end": v(-57.39, -3.2) * mm});
            skLineSegment(sketch, "E31.2.15.0", {"start": v(-63.82, -10.02) * mm, "end": v(-62.17, -11.2) * mm});
            skLineSegment(sketch, "E31.3.15.0", {"start": v(-63.3, -8.96) * mm, "end": v(-63.82, -10.02) * mm});
            skLineSegment(sketch, "E31.6.15.0", {"start": v(-63.3, -8.96) * mm, "end": v(-62.8, -7.9) * mm});
            skLineSegment(sketch, "E31.9.15.0", {"start": v(-62.8, -7.9) * mm, "end": v(-60.84, -8.45) * mm});
            skLineSegment(sketch, "E31.2.16.0", {"start": v(-65.95, -16.3) * mm, "end": v(-64.11, -17.17) * mm});
            skLineSegment(sketch, "E31.3.16.0", {"start": v(-65.63, -15.17) * mm, "end": v(-65.95, -16.3) * mm});
            skLineSegment(sketch, "E31.6.16.0", {"start": v(-65.63, -15.17) * mm, "end": v(-65.32, -14.03) * mm});
            skLineSegment(sketch, "E31.9.16.0", {"start": v(-65.32, -14.03) * mm, "end": v(-63.3, -14.22) * mm});
            skLineSegment(sketch, "E31.2.17.0", {"start": v(-66.92, -22.86) * mm, "end": v(-64.96, -23.4) * mm});
            skLineSegment(sketch, "E31.3.17.0", {"start": v(-66.82, -21.69) * mm, "end": v(-66.92, -22.86) * mm});
            skLineSegment(sketch, "E31.6.17.0", {"start": v(-66.82, -21.69) * mm, "end": v(-66.71, -20.51) * mm});
            skLineSegment(sketch, "E31.9.17.0", {"start": v(-66.71, -20.51) * mm, "end": v(-64.69, -20.34) * mm});
            skLineSegment(sketch, "E31.2.18.0", {"start": v(-66.71, -29.49) * mm, "end": v(-64.69, -29.66) * mm});
            skLineSegment(sketch, "E31.3.18.0", {"start": v(-66.82, -28.31) * mm, "end": v(-66.71, -29.49) * mm});
            skLineSegment(sketch, "E31.6.18.0", {"start": v(-66.82, -28.31) * mm, "end": v(-66.92, -27.14) * mm});
            skLineSegment(sketch, "E31.9.18.0", {"start": v(-66.92, -27.14) * mm, "end": v(-64.96, -26.6) * mm});
            skLineSegment(sketch, "E31.2.19.0", {"start": v(-65.32, -35.97) * mm, "end": v(-63.3, -35.78) * mm});
            skLineSegment(sketch, "E31.3.19.0", {"start": v(-65.63, -34.83) * mm, "end": v(-65.32, -35.97) * mm});
            skLineSegment(sketch, "E31.6.19.0", {"start": v(-65.63, -34.83) * mm, "end": v(-65.95, -33.7) * mm});
            skLineSegment(sketch, "E31.9.19.0", {"start": v(-65.95, -33.7) * mm, "end": v(-64.11, -32.83) * mm});
            skLineSegment(sketch, "E31.2.20.0", {"start": v(-62.8, -42.1) * mm, "end": v(-60.84, -41.55) * mm});
            skLineSegment(sketch, "E31.3.20.0", {"start": v(-63.3, -41.04) * mm, "end": v(-62.8, -42.1) * mm});
            skLineSegment(sketch, "E31.6.20.0", {"start": v(-63.3, -41.04) * mm, "end": v(-63.82, -39.98) * mm});
            skLineSegment(sketch, "E31.9.20.0", {"start": v(-63.82, -39.98) * mm, "end": v(-62.17, -38.8) * mm});
            skLineSegment(sketch, "E31.2.21.0", {"start": v(-59.21, -47.68) * mm, "end": v(-57.39, -46.8) * mm});
            skLineSegment(sketch, "E31.3.21.0", {"start": v(-59.9, -46.73) * mm, "end": v(-59.21, -47.68) * mm});
            skLineSegment(sketch, "E31.6.21.0", {"start": v(-59.9, -46.73) * mm, "end": v(-60.6, -45.78) * mm});
            skLineSegment(sketch, "E31.9.21.0", {"start": v(-60.6, -45.78) * mm, "end": v(-59.19, -44.31) * mm});
            skLineSegment(sketch, "E31.2.22.0", {"start": v(-54.7, -52.53) * mm, "end": v(-53.06, -51.33) * mm});
            skLineSegment(sketch, "E31.3.22.0", {"start": v(-55.55, -51.72) * mm, "end": v(-54.7, -52.53) * mm});
            skLineSegment(sketch, "E31.6.22.0", {"start": v(-55.55, -51.72) * mm, "end": v(-56.4, -50.9) * mm});
            skLineSegment(sketch, "E31.9.22.0", {"start": v(-56.4, -50.9) * mm, "end": v(-55.27, -49.22) * mm});
            skLineSegment(sketch, "E31.2.23.0", {"start": v(-49.38, -56.5) * mm, "end": v(-47.99, -55.03) * mm});
            skLineSegment(sketch, "E31.3.23.0", {"start": v(-50.36, -55.85) * mm, "end": v(-49.38, -56.5) * mm});
            skLineSegment(sketch, "E31.6.23.0", {"start": v(-50.36, -55.85) * mm, "end": v(-51.35, -55.2) * mm});
            skLineSegment(sketch, "E31.9.23.0", {"start": v(-51.35, -55.2) * mm, "end": v(-50.54, -53.34) * mm});
            skLineSegment(sketch, "E31.2.24.0", {"start": v(-43.45, -59.45) * mm, "end": v(-42.34, -57.75) * mm});
            skLineSegment(sketch, "E31.3.24.0", {"start": v(-44.53, -59) * mm, "end": v(-43.45, -59.45) * mm});
            skLineSegment(sketch, "E31.6.24.0", {"start": v(-44.53, -59) * mm, "end": v(-45.61, -58.53) * mm});
            skLineSegment(sketch, "E31.9.24.0", {"start": v(-45.61, -58.53) * mm, "end": v(-45.15, -56.55) * mm});
            skLineSegment(sketch, "E31.2.25.0", {"start": v(-37.08, -61.3) * mm, "end": v(-36.29, -59.43) * mm});
            skLineSegment(sketch, "E31.3.25.0", {"start": v(-38.23, -61.04) * mm, "end": v(-37.08, -61.3) * mm});
            skLineSegment(sketch, "E31.6.25.0", {"start": v(-38.23, -61.04) * mm, "end": v(-39.37, -60.78) * mm});
            skLineSegment(sketch, "E31.9.25.0", {"start": v(-39.37, -60.78) * mm, "end": v(-39.27, -58.75) * mm});
            skLineSegment(sketch, "E31.2.26.0", {"start": v(-30.48, -61.98) * mm, "end": v(-30.04, -60) * mm});
            skLineSegment(sketch, "E31.3.26.0", {"start": v(-31.66, -61.93) * mm, "end": v(-30.48, -61.98) * mm});
            skLineSegment(sketch, "E31.6.26.0", {"start": v(-31.66, -61.93) * mm, "end": v(-32.84, -61.88) * mm});
            skLineSegment(sketch, "E31.9.26.0", {"start": v(-32.84, -61.88) * mm, "end": v(-33.1, -59.86) * mm});
            skLineSegment(sketch, "E31.2.27.0", {"start": v(-23.87, -61.47) * mm, "end": v(-23.79, -59.44) * mm});
            skLineSegment(sketch, "E31.3.27.0", {"start": v(-25.04, -61.63) * mm, "end": v(-23.87, -61.47) * mm});
            skLineSegment(sketch, "E31.6.27.0", {"start": v(-25.04, -61.63) * mm, "end": v(-26.2, -61.8) * mm});
            skLineSegment(sketch, "E31.9.27.0", {"start": v(-26.2, -61.8) * mm, "end": v(-26.82, -59.86) * mm});
            skLineSegment(sketch, "E31.2.28.0", {"start": v(-17.46, -59.8) * mm, "end": v(-17.74, -57.78) * mm});
            skLineSegment(sketch, "E31.3.28.0", {"start": v(-18.58, -60.16) * mm, "end": v(-17.46, -59.8) * mm});
            skLineSegment(sketch, "E31.6.28.0", {"start": v(-18.58, -60.16) * mm, "end": v(-19.7, -60.52) * mm});
            skLineSegment(sketch, "E31.9.28.0", {"start": v(-19.7, -60.52) * mm, "end": v(-20.65, -58.73) * mm});
            skLineSegment(sketch, "E31.2.29.0", {"start": v(-11.45, -57) * mm, "end": v(-12.08, -55.07) * mm});
            skLineSegment(sketch, "E31.3.29.0", {"start": v(-12.48, -57.55) * mm, "end": v(-11.45, -57) * mm});
            skLineSegment(sketch, "E31.6.29.0", {"start": v(-12.48, -57.55) * mm, "end": v(-13.52, -58.11) * mm});
            skLineSegment(sketch, "E31.9.29.0", {"start": v(-13.52, -58.11) * mm, "end": v(-14.78, -56.52) * mm});
            skLineSegment(sketch, "E32.2.30.0", {"start": v(-6.03, -53.17) * mm, "end": v(-7, -51.38) * mm});
            skLineSegment(sketch, "E32.3.30.0", {"start": v(-6.95, -53.9) * mm, "end": v(-6.03, -53.17) * mm});
            skLineSegment(sketch, "E32.6.30.0", {"start": v(-6.95, -53.9) * mm, "end": v(-7.87, -54.64) * mm});
            skLineSegment(sketch, "E32.9.30.0", {"start": v(-7.87, -54.64) * mm, "end": v(-9.4, -53.3) * mm});
            skLineSegment(sketch, "E32.2.31.0", {"start": v(-1.39, -48.43) * mm, "end": v(-2.66, -46.85) * mm});
            skLineSegment(sketch, "E32.3.31.0", {"start": v(-2.16, -49.32) * mm, "end": v(-1.39, -48.43) * mm});
            skLineSegment(sketch, "E32.6.31.0", {"start": v(-2.16, -49.32) * mm, "end": v(-2.94, -50.2) * mm});
            skLineSegment(sketch, "E32.9.31.0", {"start": v(-2.94, -50.2) * mm, "end": v(-4.67, -49.16) * mm});
            skLineSegment(sketch, "E32.2.32.0", {"start": v(2.34, -42.95) * mm, "end": v(0.8, -41.62) * mm});
            skLineSegment(sketch, "E32.3.32.0", {"start": v(1.73, -43.96) * mm, "end": v(2.34, -42.95) * mm});
            skLineSegment(sketch, "E32.6.32.0", {"start": v(1.73, -43.96) * mm, "end": v(1.13, -44.97) * mm});
            skLineSegment(sketch, "E32.9.32.0", {"start": v(1.13, -44.97) * mm, "end": v(-0.77, -44.25) * mm});
            skLineSegment(sketch, "E32.2.33.0", {"start": v(5.02, -36.89) * mm, "end": v(3.27, -35.85) * mm});
            skLineSegment(sketch, "E32.3.33.0", {"start": v(4.6, -37.99) * mm, "end": v(5.02, -36.89) * mm});
            skLineSegment(sketch, "E32.6.33.0", {"start": v(4.6, -37.99) * mm, "end": v(4.2, -39.1) * mm});
            skLineSegment(sketch, "E32.9.33.0", {"start": v(4.2, -39.1) * mm, "end": v(2.2, -38.72) * mm});
            skLineSegment(sketch, "E32.2.34.0", {"start": v(6.58, -30.44) * mm, "end": v(4.68, -29.74) * mm});
            skLineSegment(sketch, "E32.3.34.0", {"start": v(6.37, -31.6) * mm, "end": v(6.58, -30.44) * mm});
            skLineSegment(sketch, "E32.6.34.0", {"start": v(6.37, -31.6) * mm, "end": v(6.16, -32.76) * mm});
            skLineSegment(sketch, "E32.9.34.0", {"start": v(6.16, -32.76) * mm, "end": v(4.13, -32.75) * mm});
            skCircle(sketch, "E33", {"center": v(-30, -25) * mm, "radius": 4 * mm});
            skSolve(sketch);
        }
        {
            var Q0;
            Q0 = qSketchRegion(id + "F11", true);
            extrude(context, id + "F12", {"entities" : qUnion([Q0]), "depth" : 10 * mm, "offsetDistance" : 25 * mm});
        }
        {
            var Q0;
            Q0=makeQuery(id+"F1.opExtrude","CAP_FACE",FACE,{"disambiguationData":[OSD([sQuery(id+"F0.wireOp",EDGE,"E0")])],"isStart":false});
            var sketch = newSketch(context, id + "F13", { "sketchPlane" : qUnion([Q0])});
            skCircle(sketch, "E34.0", {"center": v(-30, -25) * mm, "radius": 4 * mm});
            skSolve(sketch);
        }
        {
            var Q0;
            Q0 = qSketchRegion(id + "F13", true);
            extrude(context, id + "F14", {"entities" : qUnion([Q0]), "depth" : 40 * mm, "offsetDistance" : 25 * mm});
        }
        {
            var Q0;
            Q0=makeQuery(id+"F1.opExtrude","CAP_EDGE",EDGE,{"disambiguationData":[OSD([sQuery(id+"F0.wireOp",EDGE,"E0")])],"isStart":true});
            var Q1;
            Q1=makeQuery(id+"F1.opExtrude","SWEPT_FACE",FACE,{"disambiguationData":[OSD([sQuery(id+"F0.wireOp",EDGE,"E0")])]});
            chamfer(context, id + "F15", {"entities" : qUnion([Q0, Q1]), "width" : 5 * mm, "tangentPropagation" : true});
        }
        {
            var Q0;
            Q0=makeQuery(id+"F1.opExtrude","CAP_FACE",FACE,{"disambiguationData":[OSD([sQuery(id+"F0.wireOp",EDGE,"E0")])],"isStart":false});
            var sketch = newSketch(context, id + "F16", { "sketchPlane" : qUnion([Q0])});
            skCircle(sketch, "E35.0", {"center": v(-30, -25) * mm, "radius": 4 * mm});
            skSolve(sketch);
        }
        {
            var Q0;
            Q0 = qSketchRegion(id + "F16", true);
            extrude(context, id + "F17", {"entities" : qUnion([Q0]), "operationType" : NewBodyOperationType.REMOVE, "oppositeDirection" : true, "depth" : 20 * mm, "offsetDistance" : 25 * mm});
        }
        {
            var Q0;
            Q0=makeQuery(id+"F14.opExtrude","CAP_FACE",FACE,{"disambiguationData":[OSD([sQuery(id+"F13.wireOp",EDGE,"E34.0")])],"isStart":true});
            extrude(context, id + "F18", {"entities" : qUnion([Q0]), "operationType" : NewBodyOperationType.ADD, "depth" : 30 * mm, "offsetDistance" : 25 * mm});
        }
        {
            var Q0;
            Q0=makeQuery(id+"F18.opExtrude","CAP_FACE",FACE,{"disambiguationData":[OSD([sQuery(id+"F13.wireOp",EDGE,"E34.0")])],"isStart":false});
            var sketch = newSketch(context, id + "F19", { "sketchPlane" : qUnion([Q0])});
            skLineSegment(sketch, "E36.bottom", {"start": v(10, -17.5) * mm, "end": v(50, -17.5) * mm});
            skLineSegment(sketch, "E36.top", {"start": v(10, -32.5) * mm, "end": v(50, -32.5) * mm});
            skLineSegment(sketch, "E36.left", {"start": v(10, -17.5) * mm, "end": v(10, -32.5) * mm});
            skLineSegment(sketch, "E36.right", {"start": v(50, -17.5) * mm, "end": v(50, -32.5) * mm});
            skPoint(sketch, "E36.middle", {"position": v(30, -25) * mm});
            skSolve(sketch);
        }
        {
            var Q0;
            Q0 = qSketchRegion(id + "F19", true);
            extrude(context, id + "F20", {"entities" : qUnion([Q0]), "operationType" : NewBodyOperationType.ADD, "depth" : 5 * mm, "offsetDistance" : 25 * mm});
        }
        {
            var Q0;
            Q0=makeQuery(id+"F20.opExtrude","SWEPT_FACE",FACE,{"disambiguationData":[OSD([sQuery(id+"F19.wireOp",EDGE,"E36.bottom")])]});
            var sketch = newSketch(context, id + "F21", { "sketchPlane" : qUnion([Q0])});
            skLineSegment(sketch, "E37.bottom", {"start": v(-10, 15) * mm, "end": v(-18, 15) * mm});
            skLineSegment(sketch, "E37.top", {"start": v(-10, 10) * mm, "end": v(-18, 10) * mm});
            skLineSegment(sketch, "E37.left", {"start": v(-10, 15) * mm, "end": v(-10, 10) * mm});
            skLineSegment(sketch, "E37.right", {"start": v(-18, 15) * mm, "end": v(-18, 10) * mm});
            skSolve(sketch);
        }
        {
            var Q0;
            Q0 = qSketchRegion(id + "F21", true);
            extrude(context, id + "F22", {"entities" : qUnion([Q0]), "operationType" : NewBodyOperationType.ADD, "depth" : 50 * mm, "offsetDistance" : 25 * mm});
        }
        {
            var Q0;
            Q0=makeQuery(id+"F22.boolean.opBoolean","MERGE",FACE,{"derivedFrom":[makeQuery(id+"F20.opExtrude","CAP_FACE",FACE,{"disambiguationData":[OSD([sQuery(id+"F19.wireOp",EDGE,"E36.bottom"),sQuery(id+"F19.wireOp",EDGE,"E36.top"),sQuery(id+"F19.wireOp",EDGE,"E36.left"),sQuery(id+"F19.wireOp",EDGE,"E36.right")])],"isStart":false}),makeQuery(id+"F22.opExtrude","SWEPT_FACE",FACE,{"disambiguationData":[OSD([sQuery(id+"F21.wireOp",EDGE,"E37.bottom")])]})]});
            var sketch = newSketch(context, id + "F23", { "sketchPlane" : qUnion([Q0])});
            skFitSpline(sketch, "E38", {"points": [v(10, 32.5) * mm, v(14.97, 20.52) * mm, v(18, -17.5) * mm], "startDerivative": vector(19.18, -24.1) * mm, "endDerivative": vector(38, -174.37) * mm});
            skSolve(sketch);
        }
        {
            var Q0;
            Q0=makeQuery(id+"F23.imprint","IMPRINT",FACE,{"disambiguationData":[TD([[makeQuery(id+"F23.imprint","IMPRINT",EDGE,{"derivedFrom":sQuery(id+"F23.wireOp",EDGE,"E38")}),1.0]])]});
            extrude(context, id + "F24", {"entities" : qUnion([Q0]), "operationType" : NewBodyOperationType.REMOVE, "oppositeDirection" : true, "depth" : 5 * mm, "offsetDistance" : 25 * mm});
        }
        {
            var Q0;
            Q0=makeQuery(id+"F22.boolean.opBoolean","MERGE",FACE,{"derivedFrom":[makeQuery(id+"F20.opExtrude","CAP_FACE",FACE,{"disambiguationData":[OSD([sQuery(id+"F19.wireOp",EDGE,"E36.bottom"),sQuery(id+"F19.wireOp",EDGE,"E36.top"),sQuery(id+"F19.wireOp",EDGE,"E36.left"),sQuery(id+"F19.wireOp",EDGE,"E36.right")])],"isStart":false}),makeQuery(id+"F22.opExtrude","SWEPT_FACE",FACE,{"disambiguationData":[OSD([sQuery(id+"F21.wireOp",EDGE,"E37.bottom")])]})]});
            var sketch = newSketch(context, id + "F25", { "sketchPlane" : qUnion([Q0])});
            skFitSpline(sketch, "E39", {"points": [v(18, -17.5) * mm, v(34.42, -19.63) * mm, v(50, -25) * mm], "startDerivative": vector(33.2, -2.62) * mm, "endDerivative": vector(30.8, -12.38) * mm});
            skFitSpline(sketch, "E40", {"points": [v(26.33, -32.5) * mm, v(14.97, -29.73) * mm, v(10, -19.97) * mm], "startDerivative": vector(-25.49, 1.78) * mm, "endDerivative": vector(-7.08, 23.4) * mm});
            skSolve(sketch);
        }
        {
            var Q0;
            {var subQ0=sQuery(id+"F25.wireOp",EDGE,"E39");Q0=makeQuery(id+"F25.imprint","IMPRINT",FACE,{"disambiguationData":[TD([[makeQuery(id+"F25.imprint","IMPRINT",EDGE,{"derivedFrom":subQ0}),1.0]])]});}
            var Q1;
            {var subQ0=sQuery(id+"F25.wireOp",EDGE,"E40");Q1=makeQuery(id+"F25.imprint","IMPRINT",FACE,{"disambiguationData":[TD([[makeQuery(id+"F25.imprint","IMPRINT",EDGE,{"derivedFrom":subQ0}),1.0]])]});}
            extrude(context, id + "F26", {"entities" : qUnion([Q0, Q1]), "operationType" : NewBodyOperationType.REMOVE, "oppositeDirection" : true, "depth" : 5 * mm, "offsetDistance" : 25 * mm});
        }
        {
            var Q0;
            Q0=makeQuery(id+"F1.opExtrude","CAP_FACE",FACE,{"disambiguationData":[OSD([sQuery(id+"F0.wireOp",EDGE,"E0")])],"isStart":true});
            var sketch = newSketch(context, id + "F27", { "sketchPlane" : qUnion([Q0])});
            skLineSegment(sketch, "E41.bottom", {"start": v(-40, 5) * mm, "end": v(-50, 5) * mm});
            skLineSegment(sketch, "E41.top", {"start": v(-40, -5) * mm, "end": v(-50, -5) * mm});
            skLineSegment(sketch, "E41.left", {"start": v(-40, 5) * mm, "end": v(-40, -5) * mm});
            skLineSegment(sketch, "E41.right", {"start": v(-50, 5) * mm, "end": v(-50, -5) * mm});
            skPoint(sketch, "E41.middle", {"position": v(-45, 0) * mm});
            skLineSegment(sketch, "E42.1.0", {"start": v(-24.33, -32.14) * mm, "end": v(-15.67, -37.14) * mm});
            skLineSegment(sketch, "E42.1.1", {"start": v(-24.33, -32.14) * mm, "end": v(-29.33, -40.8) * mm});
            skLineSegment(sketch, "E42.1.2", {"start": v(-15.67, -37.14) * mm, "end": v(-20.67, -45.8) * mm});
            skLineSegment(sketch, "E42.1.3", {"start": v(-29.33, -40.8) * mm, "end": v(-20.67, -45.8) * mm});
            skLineSegment(sketch, "E42.2.0", {"start": v(15.67, -37.14) * mm, "end": v(24.33, -32.14) * mm});
            skLineSegment(sketch, "E42.2.1", {"start": v(15.67, -37.14) * mm, "end": v(20.67, -45.8) * mm});
            skLineSegment(sketch, "E42.2.2", {"start": v(24.33, -32.14) * mm, "end": v(29.33, -40.8) * mm});
            skLineSegment(sketch, "E42.2.3", {"start": v(20.67, -45.8) * mm, "end": v(29.33, -40.8) * mm});
            skPoint(sketch, "E42.center", {"position": v(0, 0) * mm});
            skLineSegment(sketch, "E43.2.3.0", {"start": v(40, -5) * mm, "end": v(40, 5) * mm});
            skLineSegment(sketch, "E43.3.3.0", {"start": v(40, -5) * mm, "end": v(50, -5) * mm});
            skLineSegment(sketch, "E43.6.3.0", {"start": v(40, 5) * mm, "end": v(50, 5) * mm});
            skLineSegment(sketch, "E43.9.3.0", {"start": v(50, -5) * mm, "end": v(50, 5) * mm});
            skLineSegment(sketch, "E43.2.4.0", {"start": v(24.33, 32.14) * mm, "end": v(15.67, 37.14) * mm});
            skLineSegment(sketch, "E43.3.4.0", {"start": v(24.33, 32.14) * mm, "end": v(29.33, 40.8) * mm});
            skLineSegment(sketch, "E43.6.4.0", {"start": v(15.67, 37.14) * mm, "end": v(20.67, 45.8) * mm});
            skLineSegment(sketch, "E43.9.4.0", {"start": v(29.33, 40.8) * mm, "end": v(20.67, 45.8) * mm});
            skLineSegment(sketch, "E44.2.5.0", {"start": v(-15.67, 37.14) * mm, "end": v(-24.33, 32.14) * mm});
            skLineSegment(sketch, "E44.3.5.0", {"start": v(-15.67, 37.14) * mm, "end": v(-20.67, 45.8) * mm});
            skLineSegment(sketch, "E44.6.5.0", {"start": v(-24.33, 32.14) * mm, "end": v(-29.33, 40.8) * mm});
            skLineSegment(sketch, "E44.9.5.0", {"start": v(-20.67, 45.8) * mm, "end": v(-29.33, 40.8) * mm});
            skSolve(sketch);
        }
        {
            var Q0;
            Q0 = qSketchRegion(id + "F27", true);
            extrude(context, id + "F28", {"entities" : qUnion([Q0]), "operationType" : NewBodyOperationType.REMOVE, "oppositeDirection" : true, "depth" : 4 * mm, "offsetDistance" : 25 * mm});
        }
        {
            var Q0;
            Q0=makeQuery(id+"F28.boolean.opBoolean","COPY",FACE,{"derivedFrom":makeQuery(id+"F28.opExtrude","CAP_FACE",FACE,{"disambiguationData":[OSD([sQuery(id+"F27.wireOp",EDGE,"E41.bottom"),sQuery(id+"F27.wireOp",EDGE,"E41.top"),sQuery(id+"F27.wireOp",EDGE,"E41.left"),sQuery(id+"F27.wireOp",EDGE,"E41.right")])],"isStart":false})});
            extrude(context, id + "F29", {"entities" : qUnion([Q0]), "depth" : 10 * mm, "offsetDistance" : 25 * mm});
        }
        {
            var Q0;
            Q0=makeQuery(id+"F1.opExtrude","CAP_FACE",FACE,{"disambiguationData":[OSD([sQuery(id+"F0.wireOp",EDGE,"E0")])],"isStart":false});
            var sketch = newSketch(context, id + "F30", { "sketchPlane" : qUnion([Q0])});
            skCircle(sketch, "E45.0", {"center": v(0, 40) * mm, "radius": 2 * mm});
            skSolve(sketch);
        }
        {
            var Q0;
            Q0 = qSketchRegion(id + "F30", true);
            extrude(context, id + "F31", {"entities" : qUnion([Q0]), "operationType" : NewBodyOperationType.REMOVE, "oppositeDirection" : true, "depth" : 4 * mm, "offsetDistance" : 25 * mm});
        }
        {
            var Q0;
            Q0=makeQuery(id+"F1.opExtrude","CAP_FACE",FACE,{"disambiguationData":[OSD([sQuery(id+"F0.wireOp",EDGE,"E0")])],"isStart":false});
            var sketch = newSketch(context, id + "F32", { "sketchPlane" : qUnion([Q0])});
            skCircle(sketch, "E46.0", {"center": v(30, 0) * mm, "radius": 3 * mm});
            skSolve(sketch);
        }
        {
            var Q0;
            Q0 = qSketchRegion(id + "F32", true);
            extrude(context, id + "F33", {"entities" : qUnion([Q0]), "operationType" : NewBodyOperationType.REMOVE, "oppositeDirection" : true, "depth" : 4 * mm, "offsetDistance" : 25 * mm});
        }
    });
